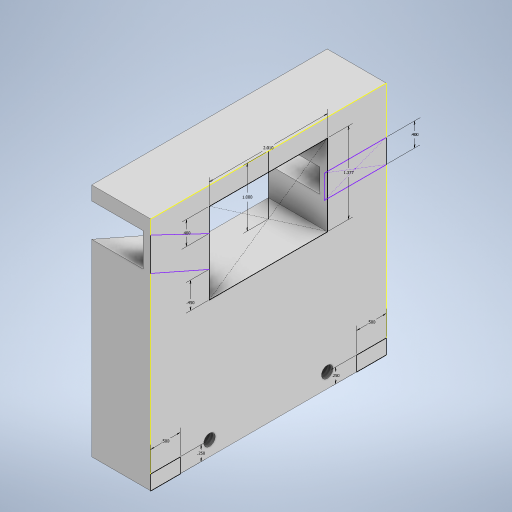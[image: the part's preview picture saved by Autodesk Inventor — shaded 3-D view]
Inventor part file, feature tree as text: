
AUTODESK INVENTOR PART (.ipt)
format: ipt  version: 2024.1 (Build 281209000, 209)  size: 279,040 bytes
history: native  units: in
note: dims shown in document units (in); Inventor stores cm internally (conversion verified against a paired STEP export)
features: extrude x3, sketch x3, hole x1
ambient origin geometry x8: Origin, YZ Plane, XZ Plane, XY Plane, X Axis, Y Axis, Z Axis, Center Point
bodies: Solid1 (feature_tree)
feature tree (7):
  extrude  "Extrusion1"  Depth=4.0in
  sketch  "Sketch2"  dims[d2=1.0in d3=0.0in d4=0.5in]
  extrude  "Extrusion2"  Depth=1.0in
  hole  "Hole1"  [1 undecoded]
  extrude  "Extrusion4"  Depth=0.125in
  sketch  "Sketch1"  dims[d0=4.0in d1=4.0in]
  sketch  "Sketch5"  dims[d5=0.25in d6=0.5in d7=0.25in d8=1.0in d9=2.01in d10=1.377in d11=1.0in d12=0.0in d13=0.196in d14=1.0in d15=0.375in d16=0.25in d17=0.5635in d18=1.0in d19=0.8108in d20=0.4in d21=0.4in d22=0.45in d28=0.125in d29=0.0in]
note: 1 required parameter value undecoded (feature->parameter linkage not recoverable at this tier; creation-order binding heuristic only, values carry confidence <= 0.55)
